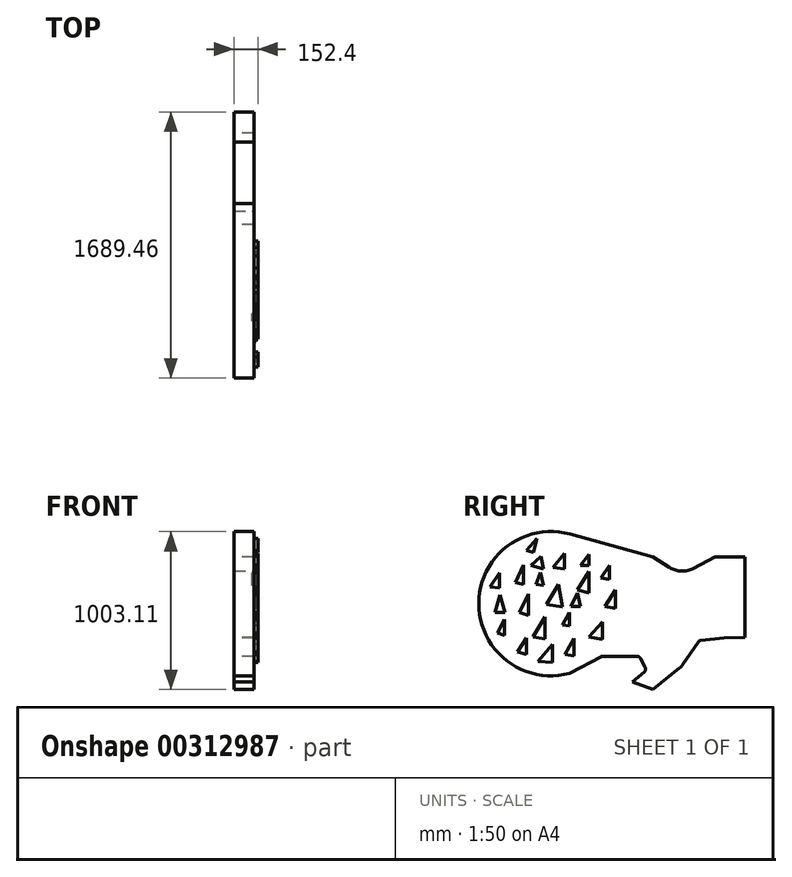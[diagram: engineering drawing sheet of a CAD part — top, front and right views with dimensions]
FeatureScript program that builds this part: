
annotation { "Feature Type Name" : "Feature", "Feature Type Description" : "" }
export const myFeature = defineFeature(function(context is Context, id is Id, definition is map)
    precondition{}
    {
        {
            var Q0;
            Q0=qCreatedBy(makeId("Right.planeOp"),FACE);
            var sketch = newSketch(context, id + "F0", { "sketchPlane" : qUnion([Q0])});
            skLineSegment(sketch, "E0", {"start": v(991.2, -160.52) * mm, "end": v(991.2, 351.19) * mm});
            skLineSegment(sketch, "E1", {"start": v(991.2, 351.19) * mm, "end": v(802.17, 351.19) * mm});
            skLineSegment(sketch, "E2", {"start": v(802.17, 351.19) * mm, "end": v(588.26, 237.33) * mm});
            skLineSegment(sketch, "E3", {"start": v(588.26, 237.33) * mm, "end": v(408.84, 351.19) * mm});
            skLineSegment(sketch, "E4", {"start": v(408.84, 351.19) * mm, "end": v(-119.05, 496.1) * mm});
            skLineSegment(sketch, "E5", {"start": v(-119.05, -387.17) * mm, "end": v(82.16, -280.08) * mm});
            skLineSegment(sketch, "E6", {"start": v(82.16, -280.08) * mm, "end": v(322.59, -280.08) * mm});
            skLineSegment(sketch, "E7", {"start": v(322.59, -280.08) * mm, "end": v(368.32, -366) * mm});
            skLineSegment(sketch, "E8", {"start": v(368.32, -366) * mm, "end": v(277.73, -442.38) * mm});
            skLineSegment(sketch, "E9", {"start": v(277.73, -442.38) * mm, "end": v(408.84, -490.68) * mm});
            skLineSegment(sketch, "E10", {"start": v(408.84, -490.68) * mm, "end": v(588.26, -345.77) * mm});
            skLineSegment(sketch, "E11", {"start": v(588.26, -345.77) * mm, "end": v(702.6, -179.52) * mm});
            skLineSegment(sketch, "E12", {"start": v(702.6, -179.52) * mm, "end": v(859.15, -161.81) * mm});
            skLineSegment(sketch, "E13", {"start": v(859.15, -161.81) * mm, "end": v(991.2, -160.52) * mm});
            skArc(sketch, "E14", {"start": v(-119.05, 496.1) * mm, "mid": v(-698.25, 54.46) * mm, "end": v(-119.05, -387.17) * mm});
            skSolve(sketch);
        }
        {
            var Q0;
            Q0 = qSketchRegion(id + "F0", true);
            extrude(context, id + "F1", {"entities" : qUnion([Q0]), "depth" : 127 * mm});
        }
        {
            var Q0;
            Q0=makeQuery(id+"F1.opExtrude","SWEPT_EDGE",EDGE,{"disambiguationData":[OSD([sQuery(id+"F0.wireOp",EDGE,"E2"),sQuery(id+"F0.wireOp",EDGE,"E3")])]});
            fillet(context, id + "F2", {"entities" : qUnion([Q0]), "radius" : 152.4 * mm, "tangentPropagation" : true, "allowEdgeOverflow" : false});
        }
        {
            var Q0;
            Q0=makeQuery(id+"F1.opExtrude","SWEPT_EDGE",EDGE,{"disambiguationData":[OSD([sQuery(id+"F0.wireOp",EDGE,"E10"),sQuery(id+"F0.wireOp",EDGE,"E11")])]});
            fillet(context, id + "F3", {"entities" : qUnion([Q0]), "radius" : 101.6 * mm, "tangentPropagation" : true, "allowEdgeOverflow" : false});
        }
        {
            var Q0;
            Q0=makeQuery(id+"F1.opExtrude","SWEPT_EDGE",EDGE,{"disambiguationData":[OSD([sQuery(id+"F0.wireOp",EDGE,"E7"),sQuery(id+"F0.wireOp",EDGE,"E8")])]});
            fillet(context, id + "F4", {"entities" : qUnion([Q0]), "radius" : 25.4 * mm, "tangentPropagation" : true, "allowEdgeOverflow" : false});
        }
        {
            var Q0;
            Q0=makeQuery(id+"F1.opExtrude","SWEPT_EDGE",EDGE,{"disambiguationData":[OSD([sQuery(id+"F0.wireOp",EDGE,"E6"),sQuery(id+"F0.wireOp",EDGE,"E7")])]});
            fillet(context, id + "F5", {"entities" : qUnion([Q0]), "radius" : 25.4 * mm, "tangentPropagation" : true, "allowEdgeOverflow" : false});
        }
        {
            var Q0;
            Q0=makeQuery(id+"F1.opExtrude","SWEPT_EDGE",EDGE,{"disambiguationData":[OSD([sQuery(id+"F0.wireOp",EDGE,"E11"),sQuery(id+"F0.wireOp",EDGE,"E12")])]});
            fillet(context, id + "F6", {"entities" : qUnion([Q0]), "radius" : 25.4 * mm, "tangentPropagation" : true, "allowEdgeOverflow" : false});
        }
        {
            var Q0;
            Q0=makeQuery(id+"F1.opExtrude","SWEPT_EDGE",EDGE,{"disambiguationData":[OSD([sQuery(id+"F0.wireOp",EDGE,"E5"),sQuery(id+"F0.wireOp",EDGE,"E6")])]});
            fillet(context, id + "F7", {"entities" : qUnion([Q0]), "radius" : 25.4 * mm, "tangentPropagation" : true, "allowEdgeOverflow" : false});
        }
        {
            var Q0;
            Q0=makeQuery(id+"F1.opExtrude","SWEPT_EDGE",EDGE,{"disambiguationData":[OSD([sQuery(id+"F0.wireOp",EDGE,"E5"),sQuery(id+"F0.wireOp",EDGE,"E14")])]});
            fillet(context, id + "F8", {"entities" : qUnion([Q0]), "radius" : 25.4 * mm, "tangentPropagation" : true, "allowEdgeOverflow" : false});
        }
        {
            var Q0;
            Q0=makeQuery(id+"F1.opExtrude","CAP_FACE",FACE,{"disambiguationData":[OSD([sQuery(id+"F0.wireOp",EDGE,"E0"),sQuery(id+"F0.wireOp",EDGE,"E1"),sQuery(id+"F0.wireOp",EDGE,"E2"),sQuery(id+"F0.wireOp",EDGE,"E3"),sQuery(id+"F0.wireOp",EDGE,"E4"),sQuery(id+"F0.wireOp",EDGE,"E5"),sQuery(id+"F0.wireOp",EDGE,"E6"),sQuery(id+"F0.wireOp",EDGE,"E7"),sQuery(id+"F0.wireOp",EDGE,"E8"),sQuery(id+"F0.wireOp",EDGE,"E9"),sQuery(id+"F0.wireOp",EDGE,"E10"),sQuery(id+"F0.wireOp",EDGE,"E11"),sQuery(id+"F0.wireOp",EDGE,"E12"),sQuery(id+"F0.wireOp",EDGE,"E13"),sQuery(id+"F0.wireOp",EDGE,"E14")])],"isStart":false});
            var sketch = newSketch(context, id + "F9", { "sketchPlane" : qUnion([Q0])});
            skLineSegment(sketch, "E15", {"start": v(-465.1, 189.04) * mm, "end": v(-415.6, 301.9) * mm});
            skLineSegment(sketch, "E16", {"start": v(-415.6, 301.9) * mm, "end": v(-415.6, 175.7) * mm});
            skLineSegment(sketch, "E17", {"start": v(-415.6, 175.7) * mm, "end": v(-465.1, 189.04) * mm});
            skSolve(sketch);
        }
        {
            var Q0;
            Q0 = qSketchRegion(id + "F9", true);
            extrude(context, id + "F10", {"entities" : qUnion([Q0]), "operationType" : NewBodyOperationType.ADD, "endBound" : BoundingType.SYMMETRIC, "depth" : 25.4 * mm});
        }
        {
            var Q0;
            Q0=makeQuery(id+"F1.opExtrude","CAP_FACE",FACE,{"disambiguationData":[OSD([sQuery(id+"F0.wireOp",EDGE,"E0"),sQuery(id+"F0.wireOp",EDGE,"E1"),sQuery(id+"F0.wireOp",EDGE,"E2"),sQuery(id+"F0.wireOp",EDGE,"E3"),sQuery(id+"F0.wireOp",EDGE,"E4"),sQuery(id+"F0.wireOp",EDGE,"E5"),sQuery(id+"F0.wireOp",EDGE,"E6"),sQuery(id+"F0.wireOp",EDGE,"E7"),sQuery(id+"F0.wireOp",EDGE,"E8"),sQuery(id+"F0.wireOp",EDGE,"E9"),sQuery(id+"F0.wireOp",EDGE,"E10"),sQuery(id+"F0.wireOp",EDGE,"E11"),sQuery(id+"F0.wireOp",EDGE,"E12"),sQuery(id+"F0.wireOp",EDGE,"E13"),sQuery(id+"F0.wireOp",EDGE,"E14")])],"isStart":false});
            var sketch = newSketch(context, id + "F11", { "sketchPlane" : qUnion([Q0])});
            skLineSegment(sketch, "E18", {"start": v(-336.4, 175.18) * mm, "end": v(-306.71, 252.4) * mm});
            skLineSegment(sketch, "E19", {"start": v(-306.71, 252.4) * mm, "end": v(-286.91, 169.24) * mm});
            skLineSegment(sketch, "E20", {"start": v(-286.91, 169.24) * mm, "end": v(-336.4, 175.18) * mm});
            skLineSegment(sketch, "E21", {"start": v(-304.49, 73.18) * mm, "end": v(-249.37, 148.13) * mm});
            skLineSegment(sketch, "E22", {"start": v(-249.37, 148.13) * mm, "end": v(-223.53, 68.11) * mm});
            skLineSegment(sketch, "E23", {"start": v(-223.53, 68.11) * mm, "end": v(-304.49, 73.18) * mm});
            skSolve(sketch);
        }
        {
            var Q0;
            Q0=makeQuery(id+"F11.imprint","IMPRINT",FACE,{"disambiguationData":[TD([[makeQuery(id+"F11.imprint","IMPRINT",EDGE,{"derivedFrom":sQuery(id+"F11.wireOp",EDGE,"E18")}),-1.0]])]});
            extrude(context, id + "F12", {"entities" : qUnion([Q0]), "endBound" : BoundingType.SYMMETRIC, "depth" : 25.4 * mm});
        }
        {
            var Q0;
            Q0=makeQuery(id+"F1.opExtrude","CAP_FACE",FACE,{"disambiguationData":[OSD([sQuery(id+"F0.wireOp",EDGE,"E0"),sQuery(id+"F0.wireOp",EDGE,"E1"),sQuery(id+"F0.wireOp",EDGE,"E2"),sQuery(id+"F0.wireOp",EDGE,"E3"),sQuery(id+"F0.wireOp",EDGE,"E4"),sQuery(id+"F0.wireOp",EDGE,"E5"),sQuery(id+"F0.wireOp",EDGE,"E6"),sQuery(id+"F0.wireOp",EDGE,"E7"),sQuery(id+"F0.wireOp",EDGE,"E8"),sQuery(id+"F0.wireOp",EDGE,"E9"),sQuery(id+"F0.wireOp",EDGE,"E10"),sQuery(id+"F0.wireOp",EDGE,"E11"),sQuery(id+"F0.wireOp",EDGE,"E12"),sQuery(id+"F0.wireOp",EDGE,"E13"),sQuery(id+"F0.wireOp",EDGE,"E14")])],"isStart":false});
            var sketch = newSketch(context, id + "F13", { "sketchPlane" : qUnion([Q0])});
            skLineSegment(sketch, "E24", {"start": v(-267.72, 49.82) * mm, "end": v(-192.22, 178) * mm});
            skLineSegment(sketch, "E25", {"start": v(-192.22, 178) * mm, "end": v(-166.52, 33.75) * mm});
            skLineSegment(sketch, "E26", {"start": v(-166.52, 33.75) * mm, "end": v(-267.72, 49.82) * mm});
            skSolve(sketch);
        }
        {
            var Q0;
            Q0=makeQuery(id+"F13.imprint","IMPRINT",FACE,{"disambiguationData":[TD([[makeQuery(id+"F13.imprint","IMPRINT",EDGE,{"derivedFrom":sQuery(id+"F13.wireOp",EDGE,"E24")}),-1.0]])]});
            extrude(context, id + "F14", {"entities" : qUnion([Q0]), "operationType" : NewBodyOperationType.ADD, "endBound" : BoundingType.SYMMETRIC, "depth" : 25.4 * mm});
        }
        {
            var Q0;
            Q0=makeQuery(id+"F1.opExtrude","CAP_FACE",FACE,{"disambiguationData":[OSD([sQuery(id+"F0.wireOp",EDGE,"E0"),sQuery(id+"F0.wireOp",EDGE,"E1"),sQuery(id+"F0.wireOp",EDGE,"E2"),sQuery(id+"F0.wireOp",EDGE,"E3"),sQuery(id+"F0.wireOp",EDGE,"E4"),sQuery(id+"F0.wireOp",EDGE,"E5"),sQuery(id+"F0.wireOp",EDGE,"E6"),sQuery(id+"F0.wireOp",EDGE,"E7"),sQuery(id+"F0.wireOp",EDGE,"E8"),sQuery(id+"F0.wireOp",EDGE,"E9"),sQuery(id+"F0.wireOp",EDGE,"E10"),sQuery(id+"F0.wireOp",EDGE,"E11"),sQuery(id+"F0.wireOp",EDGE,"E12"),sQuery(id+"F0.wireOp",EDGE,"E13"),sQuery(id+"F0.wireOp",EDGE,"E14")])],"isStart":false});
            var sketch = newSketch(context, id + "F15", { "sketchPlane" : qUnion([Q0])});
            skLineSegment(sketch, "E27", {"start": v(-354.23, -155.44) * mm, "end": v(-277.02, -28.73) * mm});
            skLineSegment(sketch, "E28", {"start": v(-277.02, -28.73) * mm, "end": v(-277.02, -169.3) * mm});
            skLineSegment(sketch, "E29", {"start": v(-277.02, -169.3) * mm, "end": v(-354.23, -155.44) * mm});
            skSolve(sketch);
        }
        {
            var Q0;
            Q0=makeQuery(id+"F15.imprint","IMPRINT",FACE,{"disambiguationData":[TD([[makeQuery(id+"F15.imprint","IMPRINT",EDGE,{"derivedFrom":sQuery(id+"F15.wireOp",EDGE,"E27")}),-1.0]])]});
            extrude(context, id + "F16", {"entities" : qUnion([Q0]), "operationType" : NewBodyOperationType.ADD, "endBound" : BoundingType.SYMMETRIC, "depth" : 50.8 * mm});
        }
        {
            var Q0;
            Q0=makeQuery(id+"F1.opExtrude","CAP_FACE",FACE,{"disambiguationData":[OSD([sQuery(id+"F0.wireOp",EDGE,"E0"),sQuery(id+"F0.wireOp",EDGE,"E1"),sQuery(id+"F0.wireOp",EDGE,"E2"),sQuery(id+"F0.wireOp",EDGE,"E3"),sQuery(id+"F0.wireOp",EDGE,"E4"),sQuery(id+"F0.wireOp",EDGE,"E5"),sQuery(id+"F0.wireOp",EDGE,"E6"),sQuery(id+"F0.wireOp",EDGE,"E7"),sQuery(id+"F0.wireOp",EDGE,"E8"),sQuery(id+"F0.wireOp",EDGE,"E9"),sQuery(id+"F0.wireOp",EDGE,"E10"),sQuery(id+"F0.wireOp",EDGE,"E11"),sQuery(id+"F0.wireOp",EDGE,"E12"),sQuery(id+"F0.wireOp",EDGE,"E13"),sQuery(id+"F0.wireOp",EDGE,"E14")])],"isStart":false});
            var sketch = newSketch(context, id + "F17", { "sketchPlane" : qUnion([Q0])});
            skLineSegment(sketch, "E30", {"start": v(-439.36, 0) * mm, "end": v(-381.94, 115.79) * mm});
            skLineSegment(sketch, "E31", {"start": v(-381.94, 115.79) * mm, "end": v(-381.94, -18.83) * mm});
            skLineSegment(sketch, "E32", {"start": v(-381.94, -18.83) * mm, "end": v(-439.36, 0) * mm});
            skSolve(sketch);
        }
        {
            var Q0;
            Q0=makeQuery(id+"F17.imprint","IMPRINT",FACE,{"disambiguationData":[TD([[makeQuery(id+"F17.imprint","IMPRINT",EDGE,{"derivedFrom":sQuery(id+"F17.wireOp",EDGE,"E30")}),-1.0]])]});
            extrude(context, id + "F18", {"entities" : qUnion([Q0]), "operationType" : NewBodyOperationType.ADD, "depth" : 25.4 * mm});
        }
        {
            var Q0;
            Q0=makeQuery(id+"F1.opExtrude","CAP_FACE",FACE,{"disambiguationData":[OSD([sQuery(id+"F0.wireOp",EDGE,"E0"),sQuery(id+"F0.wireOp",EDGE,"E1"),sQuery(id+"F0.wireOp",EDGE,"E2"),sQuery(id+"F0.wireOp",EDGE,"E3"),sQuery(id+"F0.wireOp",EDGE,"E4"),sQuery(id+"F0.wireOp",EDGE,"E5"),sQuery(id+"F0.wireOp",EDGE,"E6"),sQuery(id+"F0.wireOp",EDGE,"E7"),sQuery(id+"F0.wireOp",EDGE,"E8"),sQuery(id+"F0.wireOp",EDGE,"E9"),sQuery(id+"F0.wireOp",EDGE,"E10"),sQuery(id+"F0.wireOp",EDGE,"E11"),sQuery(id+"F0.wireOp",EDGE,"E12"),sQuery(id+"F0.wireOp",EDGE,"E13"),sQuery(id+"F0.wireOp",EDGE,"E14")])],"isStart":false});
            var sketch = newSketch(context, id + "F19", { "sketchPlane" : qUnion([Q0])});
            skLineSegment(sketch, "E33", {"start": v(-69.81, 140.6) * mm, "end": v(0, 259.12) * mm});
            skLineSegment(sketch, "E34", {"start": v(0, 259.12) * mm, "end": v(0, 123.83) * mm});
            skLineSegment(sketch, "E35", {"start": v(0, 123.83) * mm, "end": v(-69.81, 140.6) * mm});
            skLineSegment(sketch, "E36", {"start": v(102.18, 35.73) * mm, "end": v(171.4, 140.6) * mm});
            skLineSegment(sketch, "E37", {"start": v(171.4, 140.6) * mm, "end": v(171.4, 23.15) * mm});
            skLineSegment(sketch, "E38", {"start": v(171.4, 23.15) * mm, "end": v(102.18, 35.73) * mm});
            skLineSegment(sketch, "E39", {"start": v(0, -157.24) * mm, "end": v(87.5, -62.85) * mm});
            skLineSegment(sketch, "E40", {"start": v(87.5, -62.85) * mm, "end": v(87.5, -174.02) * mm});
            skLineSegment(sketch, "E41", {"start": v(87.5, -174.02) * mm, "end": v(0, -157.24) * mm});
            skLineSegment(sketch, "E42", {"start": v(-237.61, 293.72) * mm, "end": v(-151.62, 371.33) * mm});
            skLineSegment(sketch, "E43", {"start": v(-151.62, 371.33) * mm, "end": v(-151.62, 276.94) * mm});
            skLineSegment(sketch, "E44", {"start": v(-151.62, 276.94) * mm, "end": v(-237.61, 293.72) * mm});
            skSolve(sketch);
        }
        {
            var Q0;
            Q0=makeQuery(id+"F19.imprint","IMPRINT",FACE,{"disambiguationData":[TD([[makeQuery(id+"F19.imprint","IMPRINT",EDGE,{"derivedFrom":sQuery(id+"F19.wireOp",EDGE,"E33")}),-1.0]])]});
            var Q1;
            Q1=makeQuery(id+"F19.imprint","IMPRINT",FACE,{"disambiguationData":[TD([[makeQuery(id+"F19.imprint","IMPRINT",EDGE,{"derivedFrom":sQuery(id+"F19.wireOp",EDGE,"E36")}),-1.0]])]});
            var Q2;
            Q2=makeQuery(id+"F19.imprint","IMPRINT",FACE,{"disambiguationData":[TD([[makeQuery(id+"F19.imprint","IMPRINT",EDGE,{"derivedFrom":sQuery(id+"F19.wireOp",EDGE,"E39")}),-1.0]])]});
            extrude(context, id + "F20", {"entities" : qUnion([Q0, Q1, Q2]), "operationType" : NewBodyOperationType.ADD, "depth" : 25.4 * mm});
        }
        {
            var Q0;
            Q0=makeQuery(id+"F1.opExtrude","CAP_FACE",FACE,{"disambiguationData":[OSD([sQuery(id+"F0.wireOp",EDGE,"E0"),sQuery(id+"F0.wireOp",EDGE,"E1"),sQuery(id+"F0.wireOp",EDGE,"E2"),sQuery(id+"F0.wireOp",EDGE,"E3"),sQuery(id+"F0.wireOp",EDGE,"E4"),sQuery(id+"F0.wireOp",EDGE,"E5"),sQuery(id+"F0.wireOp",EDGE,"E6"),sQuery(id+"F0.wireOp",EDGE,"E7"),sQuery(id+"F0.wireOp",EDGE,"E8"),sQuery(id+"F0.wireOp",EDGE,"E9"),sQuery(id+"F0.wireOp",EDGE,"E10"),sQuery(id+"F0.wireOp",EDGE,"E11"),sQuery(id+"F0.wireOp",EDGE,"E12"),sQuery(id+"F0.wireOp",EDGE,"E13"),sQuery(id+"F0.wireOp",EDGE,"E14")])],"isStart":false});
            var sketch = newSketch(context, id + "F21", { "sketchPlane" : qUnion([Q0])});
            skLineSegment(sketch, "E45", {"start": v(-593.78, 0) * mm, "end": v(-562.1, 109.85) * mm});
            skLineSegment(sketch, "E46", {"start": v(-562.1, 109.85) * mm, "end": v(-532.4, 0) * mm});
            skLineSegment(sketch, "E47", {"start": v(-532.4, 0) * mm, "end": v(-593.78, 0) * mm});
            skLineSegment(sketch, "E48", {"start": v(-577.94, -131.68) * mm, "end": v(-534.39, -46.55) * mm});
            skLineSegment(sketch, "E49", {"start": v(-534.39, -46.55) * mm, "end": v(-534.39, -147.52) * mm});
            skLineSegment(sketch, "E50", {"start": v(-534.39, -147.52) * mm, "end": v(-577.94, -131.68) * mm});
            skLineSegment(sketch, "E51", {"start": v(-227.52, 286.05) * mm, "end": v(-154.27, 373.16) * mm});
            skLineSegment(sketch, "E52", {"start": v(-154.27, 373.16) * mm, "end": v(-154.27, 274.17) * mm});
            skLineSegment(sketch, "E53", {"start": v(-154.27, 274.17) * mm, "end": v(-227.52, 286.05) * mm});
            skLineSegment(sketch, "E54", {"start": v(-627.43, 159.34) * mm, "end": v(-566.06, 248.43) * mm});
            skLineSegment(sketch, "E55", {"start": v(-566.06, 248.43) * mm, "end": v(-566.06, 153.4) * mm});
            skLineSegment(sketch, "E56", {"start": v(-566.06, 153.4) * mm, "end": v(-627.43, 159.34) * mm});
            skLineSegment(sketch, "E57", {"start": v(-393.82, 390.98) * mm, "end": v(-328.49, 470.17) * mm});
            skLineSegment(sketch, "E58", {"start": v(-328.49, 470.17) * mm, "end": v(-352.25, 379.1) * mm});
            skLineSegment(sketch, "E59", {"start": v(-352.25, 379.1) * mm, "end": v(-393.82, 390.98) * mm});
            skLineSegment(sketch, "E60", {"start": v(-322.55, -311.84) * mm, "end": v(-229.5, -204.93) * mm});
            skLineSegment(sketch, "E61", {"start": v(-229.5, -204.93) * mm, "end": v(-229.5, -317.78) * mm});
            skLineSegment(sketch, "E62", {"start": v(-229.5, -317.78) * mm, "end": v(-322.55, -311.84) * mm});
            skLineSegment(sketch, "E63", {"start": v(-168.13, -80.2) * mm, "end": v(-120.88, 0) * mm});
            skLineSegment(sketch, "E64", {"start": v(-120.88, 0) * mm, "end": v(-120.88, -88.13) * mm});
            skLineSegment(sketch, "E65", {"start": v(-120.88, -88.13) * mm, "end": v(-168.13, -80.2) * mm});
            skLineSegment(sketch, "E66", {"start": v(-51.32, 297.93) * mm, "end": v(0, 367.22) * mm});
            skLineSegment(sketch, "E67", {"start": v(0, 367.22) * mm, "end": v(0, 297.93) * mm});
            skLineSegment(sketch, "E68", {"start": v(0, 297.93) * mm, "end": v(-51.32, 297.93) * mm});
            skLineSegment(sketch, "E69", {"start": v(77.36, 216.76) * mm, "end": v(130.94, 297.93) * mm});
            skLineSegment(sketch, "E70", {"start": v(130.94, 297.93) * mm, "end": v(130.94, 208.84) * mm});
            skLineSegment(sketch, "E71", {"start": v(130.94, 208.84) * mm, "end": v(77.36, 216.76) * mm});
            skLineSegment(sketch, "E72", {"start": v(-150.31, -268.29) * mm, "end": v(-92.9, -165.34) * mm});
            skLineSegment(sketch, "E73", {"start": v(-92.9, -165.34) * mm, "end": v(-92.9, -276.2) * mm});
            skLineSegment(sketch, "E74", {"start": v(-92.9, -276.2) * mm, "end": v(-150.31, -268.29) * mm});
            skLineSegment(sketch, "E75", {"start": v(-451.23, -250.47) * mm, "end": v(-395.8, -163.36) * mm});
            skLineSegment(sketch, "E76", {"start": v(-395.8, -163.36) * mm, "end": v(-395.8, -268.29) * mm});
            skLineSegment(sketch, "E77", {"start": v(-395.8, -268.29) * mm, "end": v(-451.23, -250.47) * mm});
            skLineSegment(sketch, "E78", {"start": v(-112.7, 35.73) * mm, "end": v(-69.81, 123.83) * mm});
            skLineSegment(sketch, "E79", {"start": v(-69.81, 123.83) * mm, "end": v(-51.32, 35.73) * mm});
            skLineSegment(sketch, "E80", {"start": v(-51.32, 35.73) * mm, "end": v(-112.7, 35.73) * mm});
            skLineSegment(sketch, "E81", {"start": v(-366.1, 297.93) * mm, "end": v(-302.75, 353.36) * mm});
            skLineSegment(sketch, "E82", {"start": v(-302.75, 353.36) * mm, "end": v(-288.9, 274.17) * mm});
            skLineSegment(sketch, "E83", {"start": v(-288.9, 274.17) * mm, "end": v(-366.1, 297.93) * mm});
            skSolve(sketch);
        }
        {
            var Q0;
            Q0=makeQuery(id+"F21.imprint","IMPRINT",FACE,{"disambiguationData":[TD([[makeQuery(id+"F21.imprint","IMPRINT",EDGE,{"derivedFrom":sQuery(id+"F21.wireOp",EDGE,"E45")}),-1.0]])]});
            var Q1;
            Q1=makeQuery(id+"F21.imprint","IMPRINT",FACE,{"disambiguationData":[TD([[makeQuery(id+"F21.imprint","IMPRINT",EDGE,{"derivedFrom":sQuery(id+"F21.wireOp",EDGE,"E48")}),-1.0]])]});
            var Q2;
            Q2=makeQuery(id+"F21.imprint","IMPRINT",FACE,{"disambiguationData":[TD([[makeQuery(id+"F21.imprint","IMPRINT",EDGE,{"derivedFrom":sQuery(id+"F21.wireOp",EDGE,"E75")}),-1.0]])]});
            var Q3;
            Q3=makeQuery(id+"F21.imprint","IMPRINT",FACE,{"disambiguationData":[TD([[makeQuery(id+"F21.imprint","IMPRINT",EDGE,{"derivedFrom":sQuery(id+"F21.wireOp",EDGE,"E60")}),-1.0]])]});
            var Q4;
            Q4=makeQuery(id+"F21.imprint","IMPRINT",FACE,{"disambiguationData":[TD([[makeQuery(id+"F21.imprint","IMPRINT",EDGE,{"derivedFrom":sQuery(id+"F21.wireOp",EDGE,"E72")}),-1.0]])]});
            var Q5;
            Q5=makeQuery(id+"F21.imprint","IMPRINT",FACE,{"disambiguationData":[TD([[makeQuery(id+"F21.imprint","IMPRINT",EDGE,{"derivedFrom":sQuery(id+"F21.wireOp",EDGE,"E63")}),-1.0]])]});
            var Q6;
            Q6=makeQuery(id+"F21.imprint","IMPRINT",FACE,{"disambiguationData":[TD([[makeQuery(id+"F21.imprint","IMPRINT",EDGE,{"derivedFrom":sQuery(id+"F21.wireOp",EDGE,"E78")}),-1.0]])]});
            var Q7;
            Q7=makeQuery(id+"F21.imprint","IMPRINT",FACE,{"disambiguationData":[TD([[makeQuery(id+"F21.imprint","IMPRINT",EDGE,{"derivedFrom":sQuery(id+"F21.wireOp",EDGE,"E51")}),-1.0]])]});
            var Q8;
            Q8=makeQuery(id+"F21.imprint","IMPRINT",FACE,{"disambiguationData":[TD([[makeQuery(id+"F21.imprint","IMPRINT",EDGE,{"derivedFrom":sQuery(id+"F21.wireOp",EDGE,"E81")}),-1.0]])]});
            var Q9;
            Q9=makeQuery(id+"F21.imprint","IMPRINT",FACE,{"disambiguationData":[TD([[makeQuery(id+"F21.imprint","IMPRINT",EDGE,{"derivedFrom":sQuery(id+"F21.wireOp",EDGE,"E57")}),-1.0]])]});
            var Q10;
            Q10=makeQuery(id+"F21.imprint","IMPRINT",FACE,{"disambiguationData":[TD([[makeQuery(id+"F21.imprint","IMPRINT",EDGE,{"derivedFrom":sQuery(id+"F21.wireOp",EDGE,"E66")}),-1.0]])]});
            var Q11;
            Q11=makeQuery(id+"F21.imprint","IMPRINT",FACE,{"disambiguationData":[TD([[makeQuery(id+"F21.imprint","IMPRINT",EDGE,{"derivedFrom":sQuery(id+"F21.wireOp",EDGE,"E69")}),-1.0]])]});
            var Q12;
            Q12=makeQuery(id+"F21.imprint","IMPRINT",FACE,{"disambiguationData":[TD([[makeQuery(id+"F21.imprint","IMPRINT",EDGE,{"derivedFrom":sQuery(id+"F21.wireOp",EDGE,"E54")}),-1.0]])]});
            extrude(context, id + "F22", {"entities" : qUnion([Q0, Q1, Q2, Q3, Q4, Q5, Q6, Q7, Q8, Q9, Q10, Q11, Q12]), "operationType" : NewBodyOperationType.ADD, "depth" : 25.4 * mm});
        }
    });
